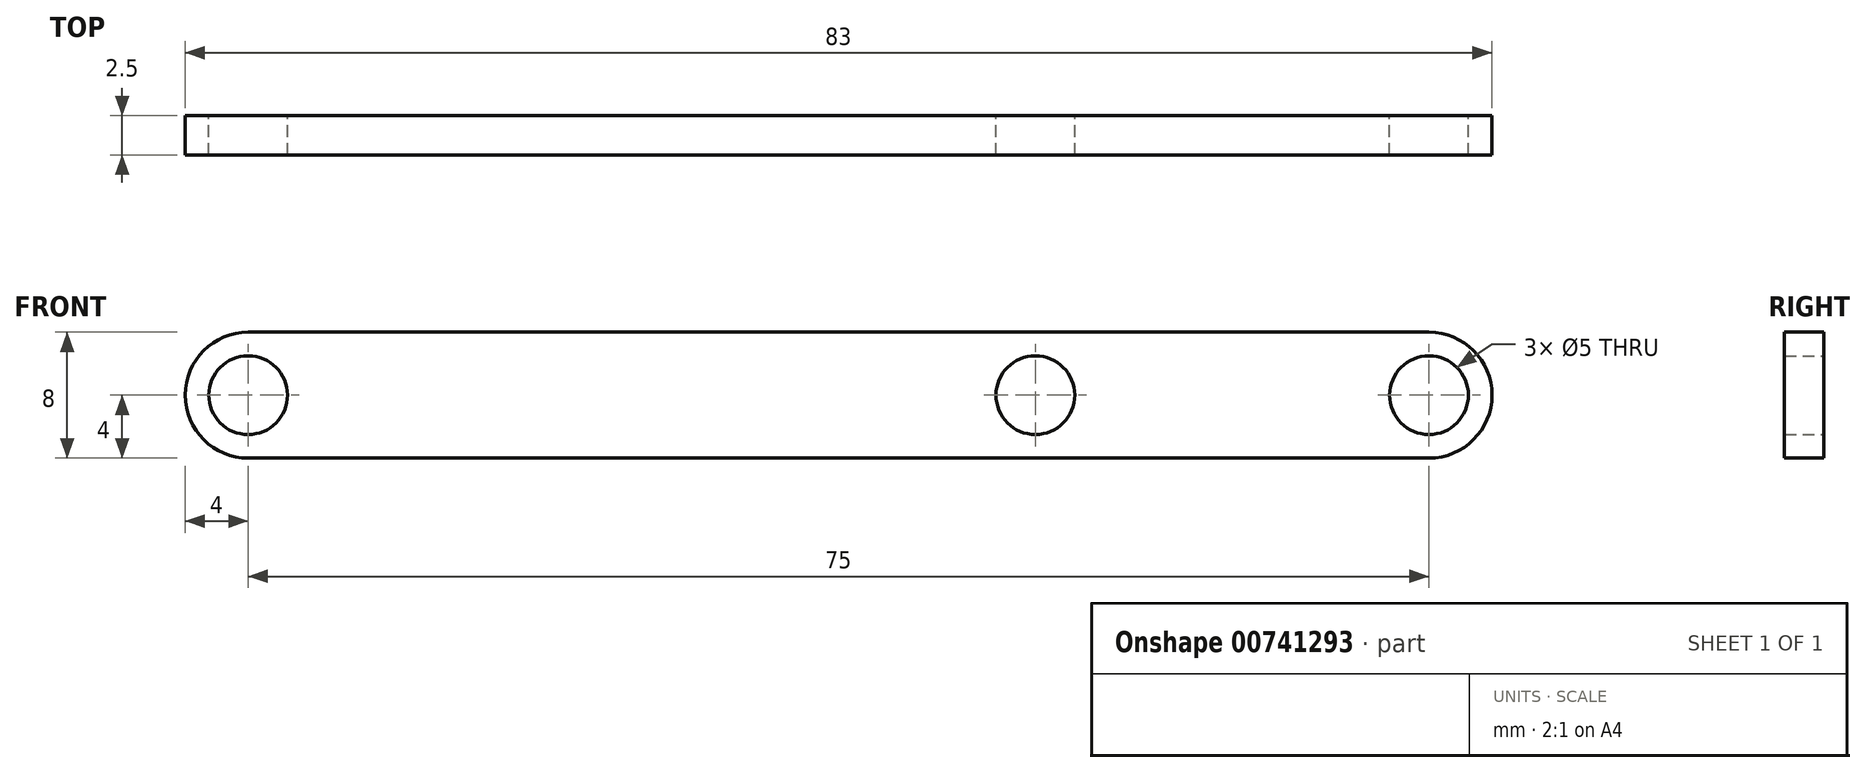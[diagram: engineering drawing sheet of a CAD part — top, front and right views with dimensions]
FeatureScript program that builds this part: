
annotation { "Feature Type Name" : "Feature", "Feature Type Description" : "" }
export const myFeature = defineFeature(function(context is Context, id is Id, definition is map)
    precondition{}
    {
        {
            var Q0;
            Q0=qCreatedBy(makeId("Front.planeOp"),FACE);
            var sketch = newSketch(context, id + "F0", { "sketchPlane" : qUnion([Q0])});
            skArc(sketch, "E0", {"start": v(0, 4) * mm, "mid": v(-4, 0) * mm, "end": v(0, -4) * mm});
            skCircle(sketch, "E1", {"center": v(0, 0) * mm, "radius": 2.5 * mm});
            skLineSegment(sketch, "E2", {"start": v(0, 0) * mm, "end": v(75, 0) * mm, "construction": true});
            skCircle(sketch, "E3", {"center": v(75, 0) * mm, "radius": 2.5 * mm});
            skArc(sketch, "E4", {"start": v(75, -4) * mm, "mid": v(79, 0) * mm, "end": v(75, 4) * mm});
            skLineSegment(sketch, "E5", {"start": v(0, -4) * mm, "end": v(75, -4) * mm});
            skLineSegment(sketch, "E6", {"start": v(0, 4) * mm, "end": v(75, 4) * mm});
            skCircle(sketch, "E7", {"center": v(50, 0) * mm, "radius": 2.5 * mm});
            skSolve(sketch);
        }
        {
            var Q0;
            Q0=makeQuery(id+"F0.imprint","IMPRINT",FACE,{"disambiguationData":[TD([[makeQuery(id+"F0.imprint","IMPRINT",EDGE,{"derivedFrom":sQuery(id+"F0.wireOp",EDGE,"E0")}),1.0]])]});
            extrude(context, id + "F1", {"entities" : qUnion([Q0]), "depth" : 2.5 * mm, "offsetDistance" : 25.4 * mm});
        }
    });
